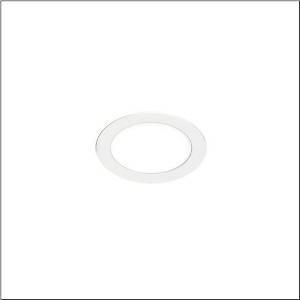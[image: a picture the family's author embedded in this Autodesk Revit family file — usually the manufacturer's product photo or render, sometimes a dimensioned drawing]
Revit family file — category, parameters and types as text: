
# Revit family: lunis_41_flat_51dr107dgba
name_source: partatom
category: Lighting Fixtures
units: mm (PartAtom-declared; Revit-internal decimal feet)

## family parameters
Cut with Voids When Loaded = No
Host = Face
Light Source = No
Part Type = Normal
Room Calculation Point = No
Round Connector Dimension = Use Diameter
Shared = No

## types (1)
- --- (1 x LED, 1360 lm, 15 W, 4000K)
    Apparent Load = 15 VA
    CIE Flux Codes = 49 80 96 100 100
    Color Rendering = 80
    Color Temperature = 4000K
    Default Elevation = 1800 mm
    Description = Lunis 41,  flat, downlight, light emission: direct distribution, LED rated luminous flux: 1.250lm, light colour: 830/840, control gear: ECG, mains connection: 230V, AC, 50/60Hz, housing, round, of aluminium, coated, traffic white (RAL 9016), diameter: 170mm, protection rating (complete): IP20, insulation class (complete): insulation class II (safety insulation), certification: CE, permissible ambient temperature for indoor applications: -20..+40°C, packaging unit: 1 piece
    Height = 0 mm  [stored 0 ft]
    Lamp = 1 x LED
    Lamp Light Flux = 1360 lm
    Lamp Power = 15 W
    Lamp count = 1
    Length = 170 mm  [stored 0.557743 ft]
    Luminous efficacy = 91 lm/W
    Manufacturer = Siteco
    ModVariant = No
    Model = 51DR107DGBA
    Mounting Place = Ceiling
    Mounting Type = Recessed
    Number of Poles = 1
    OnlyDefault = Yes
    Power Factor = 1
    Product Name = Lunis 41 flat
    Product group = downlight | ceiling recessed
    ProductGroupID = 402
    Protection Class = Protection class II
    Protection Degree = IP 20
    RLX_Detail_Level = 1
    RlxData = <blob elided: 24241 chars, md5=5a6b811d>
    Socket = socket
    Standby Power = 0 W
    System Light Flux = 1360 lm
    System Power = 15 W
    Type Comments = factory setting: colour temperature 4000K
    Type Image = l_1007045.jpg
    URL = http://relux.com
    VarID = @adj_117321
    Voltage = 0 V
    Weight = 0.00 kg
    Width = 0 mm  [stored 0 ft]

note: [stored X ft] marks values corroborated as IEEE doubles in the binary element streams (Revit-internal decimal feet)

## geometry (parser evidence)
native form markers: Blend x4, Sweep x12
no freeform markers — native parametric forms only
